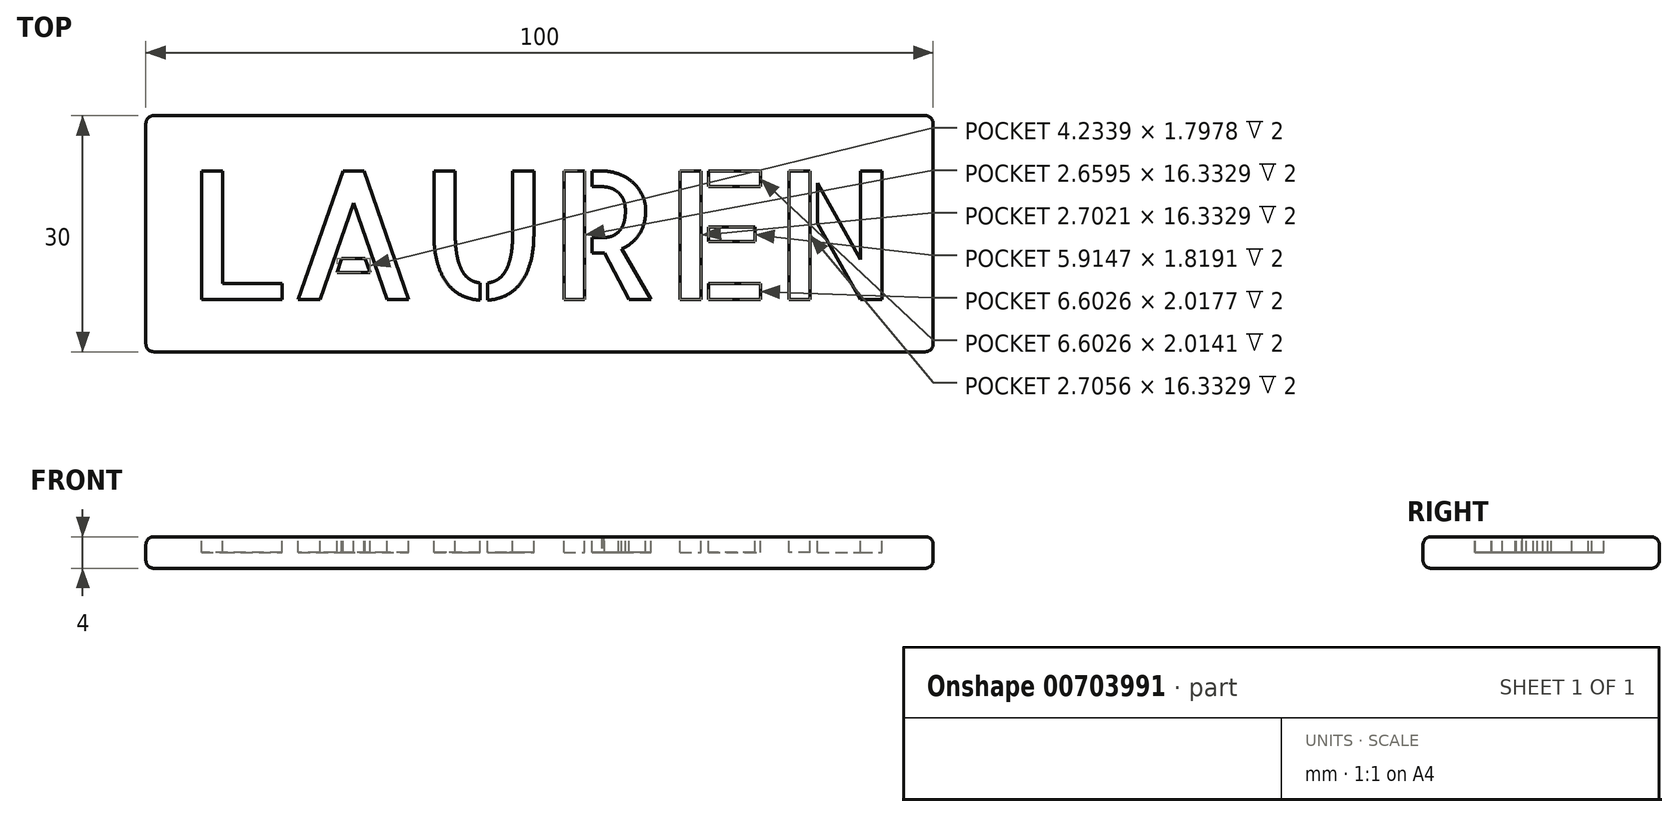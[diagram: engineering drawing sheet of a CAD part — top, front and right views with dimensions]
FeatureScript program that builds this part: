
annotation { "Feature Type Name" : "Feature", "Feature Type Description" : "" }
export const myFeature = defineFeature(function(context is Context, id is Id, definition is map)
    precondition{}
    {
        {
            var Q0;
            Q0=qCreatedBy(makeId("Top.planeOp"),FACE);
            var sketch = newSketch(context, id + "F0", { "sketchPlane" : qUnion([Q0])});
            skLineSegment(sketch, "E0.bottom", {"start": v(50, 15) * mm, "end": v(-50, 15) * mm});
            skLineSegment(sketch, "E0.top", {"start": v(50, -15) * mm, "end": v(-50, -15) * mm});
            skLineSegment(sketch, "E0.left", {"start": v(50, 15) * mm, "end": v(50, -15) * mm});
            skLineSegment(sketch, "E0.right", {"start": v(-50, 15) * mm, "end": v(-50, -15) * mm});
            skPoint(sketch, "E0.middle", {"position": v(0, 0) * mm});
            skSolve(sketch);
        }
        {
            var Q0;
            Q0=makeQuery(id+"F0.imprint","IMPRINT",FACE,{"disambiguationData":[TD([[makeQuery(id+"F0.imprint","IMPRINT",EDGE,{"derivedFrom":sQuery(id+"F0.wireOp",EDGE,"E0.bottom")}),1.0]])]});
            extrude(context, id + "F1", {"entities" : qUnion([Q0]), "oppositeDirection" : true, "depth" : 4 * mm, "offsetDistance" : 25 * mm});
        }
        {
            var Q0;
            Q0=makeQuery(id+"F1.opExtrude","CAP_EDGE",EDGE,{"disambiguationData":[OSD([sQuery(id+"F0.wireOp",EDGE,"E0.bottom")])],"isStart":true});
            var Q1;
            Q1=makeQuery(id+"F1.opExtrude","CAP_EDGE",EDGE,{"disambiguationData":[OSD([sQuery(id+"F0.wireOp",EDGE,"E0.bottom")])],"isStart":false});
            var Q2;
            Q2=makeQuery(id+"F1.opExtrude","CAP_EDGE",EDGE,{"disambiguationData":[OSD([sQuery(id+"F0.wireOp",EDGE,"E0.right")])],"isStart":true});
            var Q3;
            Q3=makeQuery(id+"F1.opExtrude","CAP_EDGE",EDGE,{"disambiguationData":[OSD([sQuery(id+"F0.wireOp",EDGE,"E0.right")])],"isStart":false});
            var Q4;
            Q4=makeQuery(id+"F1.opExtrude","SWEPT_EDGE",EDGE,{"disambiguationData":[OSD([sQuery(id+"F0.wireOp",EDGE,"E0.bottom"),sQuery(id+"F0.wireOp",EDGE,"E0.right")])]});
            var Q5;
            Q5=makeQuery(id+"F1.opExtrude","SWEPT_EDGE",EDGE,{"disambiguationData":[OSD([sQuery(id+"F0.wireOp",EDGE,"E0.bottom"),sQuery(id+"F0.wireOp",EDGE,"E0.left")])]});
            var Q6;
            Q6=makeQuery(id+"F1.opExtrude","CAP_EDGE",EDGE,{"disambiguationData":[OSD([sQuery(id+"F0.wireOp",EDGE,"E0.left")])],"isStart":false});
            var Q7;
            Q7=makeQuery(id+"F1.opExtrude","CAP_EDGE",EDGE,{"disambiguationData":[OSD([sQuery(id+"F0.wireOp",EDGE,"E0.left")])],"isStart":true});
            var Q8;
            Q8=makeQuery(id+"F1.opExtrude","SWEPT_EDGE",EDGE,{"disambiguationData":[OSD([sQuery(id+"F0.wireOp",EDGE,"E0.top"),sQuery(id+"F0.wireOp",EDGE,"E0.left")])]});
            var Q9;
            Q9=makeQuery(id+"F1.opExtrude","CAP_EDGE",EDGE,{"disambiguationData":[OSD([sQuery(id+"F0.wireOp",EDGE,"E0.top")])],"isStart":false});
            var Q10;
            Q10=makeQuery(id+"F1.opExtrude","CAP_EDGE",EDGE,{"disambiguationData":[OSD([sQuery(id+"F0.wireOp",EDGE,"E0.top")])],"isStart":true});
            var Q11;
            Q11=makeQuery(id+"F1.opExtrude","SWEPT_EDGE",EDGE,{"disambiguationData":[OSD([sQuery(id+"F0.wireOp",EDGE,"E0.top"),sQuery(id+"F0.wireOp",EDGE,"E0.right")])]});
            fillet(context, id + "F2", {"entities" : qUnion([Q0, Q1, Q2, Q3, Q4, Q5, Q6, Q7, Q8, Q9, Q10, Q11]), "radius" : 1 * mm, "tangentPropagation" : true, "allowEdgeOverflow" : false});
        }
        {
            var Q0;
            Q0=qCreatedBy(makeId("Top.planeOp"),FACE);
            var sketch = newSketch(context, id + "F3", { "sketchPlane" : qUnion([Q0])});
            skText(sketch, "E1", { "text": "LAUREN", "fontName": "AllertaStencil-Regular.ttf"});
            const initialGuessF3  = {"E1": [-0.045, -0.00834, 1, 0, 0.01634]};
            skSetInitialGuess(sketch, initialGuessF3);
            skSolve(sketch);
        }
        {
            var Q0;
            Q0 = qSketchRegion(id + "F3", true);
            extrude(context, id + "F4", {"entities" : qUnion([Q0]), "operationType" : NewBodyOperationType.REMOVE, "oppositeDirection" : true, "depth" : 2 * mm, "offsetDistance" : 25 * mm});
        }
    });
